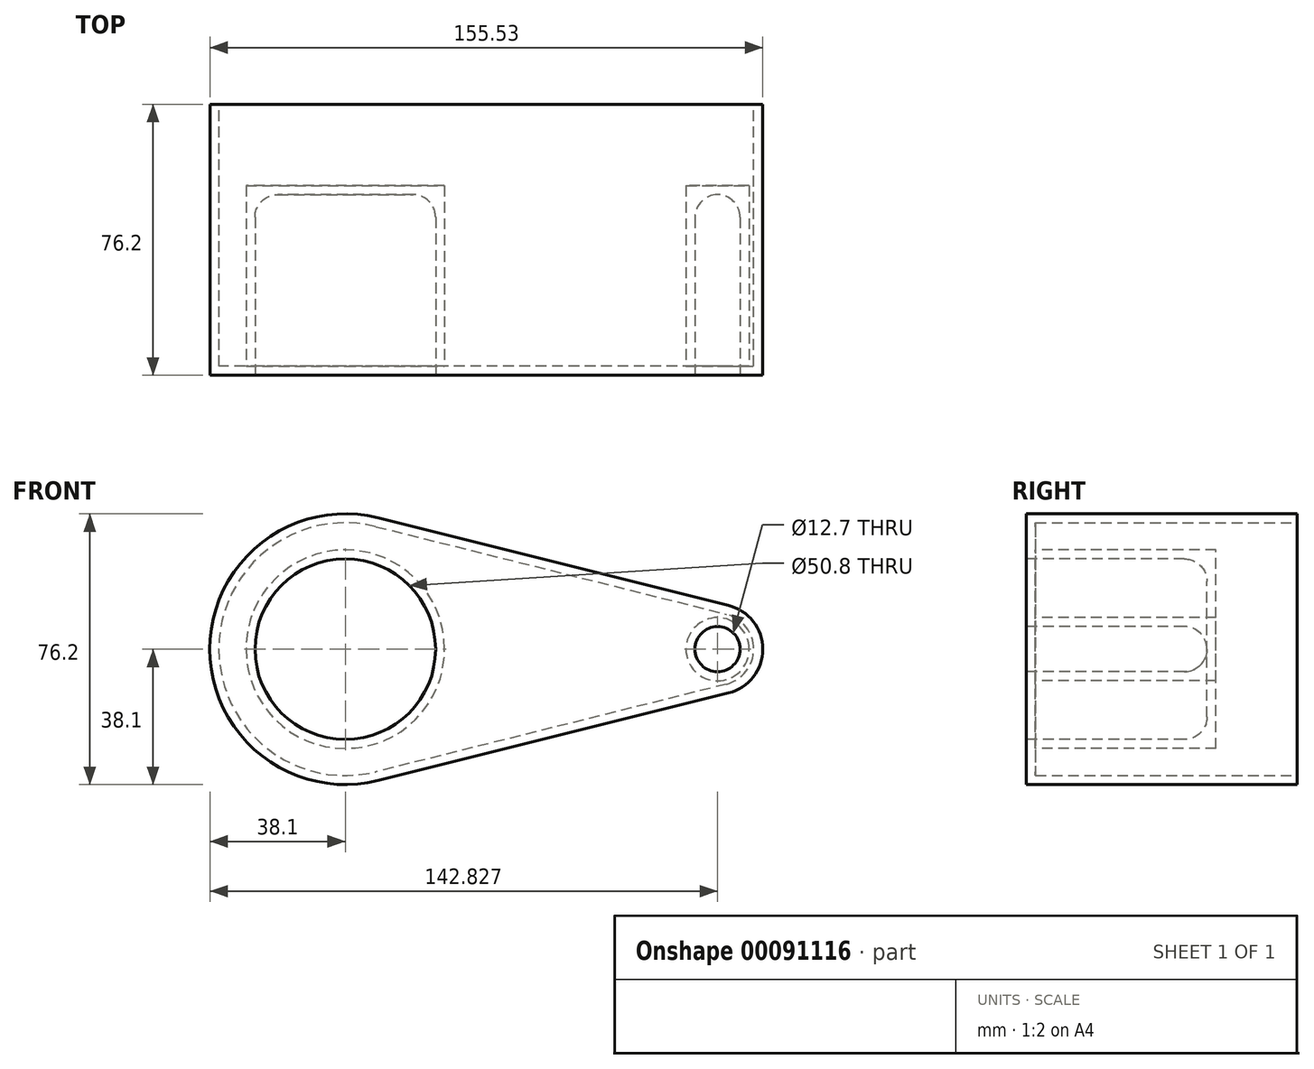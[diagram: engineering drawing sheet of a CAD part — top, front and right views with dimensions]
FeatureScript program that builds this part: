
annotation { "Feature Type Name" : "Feature", "Feature Type Description" : "" }
export const myFeature = defineFeature(function(context is Context, id is Id, definition is map)
    precondition{}
    {
        {
            var Q0;
            Q0=qCreatedBy(makeId("Front.planeOp"),FACE);
            var sketch = newSketch(context, id + "F4", { "sketchPlane" : qUnion([Q0])});
            skCircle(sketch, "E0", {"center": v(0, 0) * mm, "radius": 38.1 * mm});
            skCircle(sketch, "E1", {"center": v(104.73, 0) * mm, "radius": 12.7 * mm});
            skLineSegment(sketch, "E2", {"start": v(9.24, 36.96) * mm, "end": v(107.8, 12.32) * mm});
            skLineSegment(sketch, "E3", {"start": v(107.8, -12.32) * mm, "end": v(9.24, -36.96) * mm});
            skSolve(sketch);
        }
        {
            var Q0;
            {var subQ0=sQuery(id+"F4.wireOp",EDGE,"E0");var subQ1=makeQuery(id+"F4.imprint","INTERSECT",VERTEX,{"derivedFrom":[subQ0,sQuery(id+"F4.wireOp",EDGE,"E2")]});Q0=makeQuery(id+"F4.imprint","IMPRINT",FACE,{"disambiguationData":[TD([[makeQuery(id+"F4.imprint","IMPRINT",EDGE,{"disambiguationData":[TD([[subQ1,-1.0]])],"derivedFrom":subQ0}),1.0]])]});}
            var Q1;
            {var subQ0=sQuery(id+"F4.wireOp",EDGE,"E2");Q1=makeQuery(id+"F4.imprint","IMPRINT",FACE,{"disambiguationData":[TD([[makeQuery(id+"F4.imprint","IMPRINT",EDGE,{"derivedFrom":subQ0}),-1.0]])]});}
            var Q2;
            {var subQ0=sQuery(id+"F4.wireOp",EDGE,"E1");var subQ1=makeQuery(id+"F4.imprint","INTERSECT",VERTEX,{"derivedFrom":[subQ0,sQuery(id+"F4.wireOp",EDGE,"E2")]});Q2=makeQuery(id+"F4.imprint","IMPRINT",FACE,{"disambiguationData":[TD([[makeQuery(id+"F4.imprint","IMPRINT",EDGE,{"disambiguationData":[TD([[subQ1,-1.0]])],"derivedFrom":subQ0}),1.0]])]});}
            extrude(context, id + "F5", {"entities" : qUnion([Q0, Q1, Q2]), "depth" : 76.2 * mm});
        }
        {
            var Q0;
            Q0=makeQuery(id+"F5.opExtrude","CAP_FACE",FACE,{"disambiguationData":[OSD([sQuery(id+"F4.wireOp",EDGE,"E0"),sQuery(id+"F4.wireOp",EDGE,"E1"),sQuery(id+"F4.wireOp",EDGE,"E2"),sQuery(id+"F4.wireOp",EDGE,"E3")])],"isStart":false});
            var sketch = newSketch(context, id + "F6", { "sketchPlane" : qUnion([Q0])});
            skCircle(sketch, "E4", {"center": v(0, 0) * mm, "radius": 25.4 * mm});
            skCircle(sketch, "E5", {"center": v(104.73, 0) * mm, "radius": 6.35 * mm});
            skSolve(sketch);
        }
        {
            var Q0;
            Q0=makeQuery(id+"F6.imprint","IMPRINT",FACE,{"disambiguationData":[TD([[makeQuery(id+"F6.imprint","IMPRINT",EDGE,{"derivedFrom":sQuery(id+"F6.wireOp",EDGE,"E4")}),1.0]])]});
            var Q1;
            Q1=makeQuery(id+"F6.imprint","IMPRINT",FACE,{"disambiguationData":[TD([[makeQuery(id+"F6.imprint","IMPRINT",EDGE,{"derivedFrom":sQuery(id+"F6.wireOp",EDGE,"E5")}),1.0]])]});
            extrude(context, id + "F0", {"entities" : qUnion([Q0, Q1]), "operationType" : NewBodyOperationType.REMOVE, "oppositeDirection" : true, "depth" : 50.8 * mm});
        }
        {
            var Q0;
            Q0=makeQuery(id+"F5.opExtrude","CAP_FACE",FACE,{"disambiguationData":[OSD([sQuery(id+"F4.wireOp",EDGE,"E0"),sQuery(id+"F4.wireOp",EDGE,"E1"),sQuery(id+"F4.wireOp",EDGE,"E2"),sQuery(id+"F4.wireOp",EDGE,"E3")])],"isStart":true});
            shell(context, id + "F1", {"entities" : qUnion([Q0]), "thickness" : 2.54 * mm});
        }
        {
            var Q0;
            Q0=makeQuery(id+"F0.boolean.opBoolean","COPY",EDGE,{"derivedFrom":makeQuery(id+"F0.opExtrude","CAP_EDGE",EDGE,{"disambiguationData":[OSD([sQuery(id+"F6.wireOp",EDGE,"E4")])],"isStart":true})});
            var Q1;
            Q1=makeQuery(id+"F0.boolean.opBoolean","COPY",EDGE,{"derivedFrom":makeQuery(id+"F0.opExtrude","CAP_EDGE",EDGE,{"disambiguationData":[OSD([sQuery(id+"F6.wireOp",EDGE,"E5")])],"isStart":true})});
            var Q2;
            Q2=makeQuery(id+"F0.boolean.opBoolean","COPY",EDGE,{"derivedFrom":makeQuery(id+"F0.opExtrude","CAP_EDGE",EDGE,{"disambiguationData":[OSD([sQuery(id+"F6.wireOp",EDGE,"E4")])],"isStart":false})});
            var Q3;
            Q3=makeQuery(id+"F0.boolean.opBoolean","COPY",EDGE,{"derivedFrom":makeQuery(id+"F0.opExtrude","CAP_EDGE",EDGE,{"disambiguationData":[OSD([sQuery(id+"F6.wireOp",EDGE,"E5")])],"isStart":false})});
            fillet(context, id + "F2", {"entities" : qUnion([Q0, Q1, Q2, Q3]), "radius" : 6.35 * mm, "tangentPropagation" : true, "allowEdgeOverflow" : false});
        }
    });
